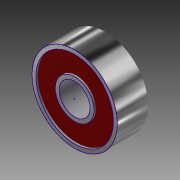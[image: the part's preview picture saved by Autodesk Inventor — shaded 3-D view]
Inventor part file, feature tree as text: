
AUTODESK INVENTOR PART (.ipt)
format: ipt  version: 2014 SP2 (Build 180246200, 246)  size: 118,272 bytes
history: native  units: mm
features: extrude x4, sketch x1
ambient origin geometry x8: Origin, YZ Plane, XZ Plane, XY Plane, X Axis, Y Axis, Z Axis, Center Point
bodies: Solid1 (feature_tree)
feature tree (5):
  sketch  "Sketch1"  dims[d0=8.0mm d1=10.0mm d2=22.0mm d3=20.0mm d4=7.5mm d5=0.0mm d6=8.0mm d7=0.0mm d8=0.5mm d9=0.0mm d10=8.0mm d11=0.0mm]
  extrude  "Extrusion1"  Depth=10.0mm
  extrude  "Extrusion2"  Depth=8.0mm
  extrude  "Extrusion3"  Depth=8.0mm
  extrude  "Extrusion4"  Depth=7.5mm TaperAngle=0.0deg
